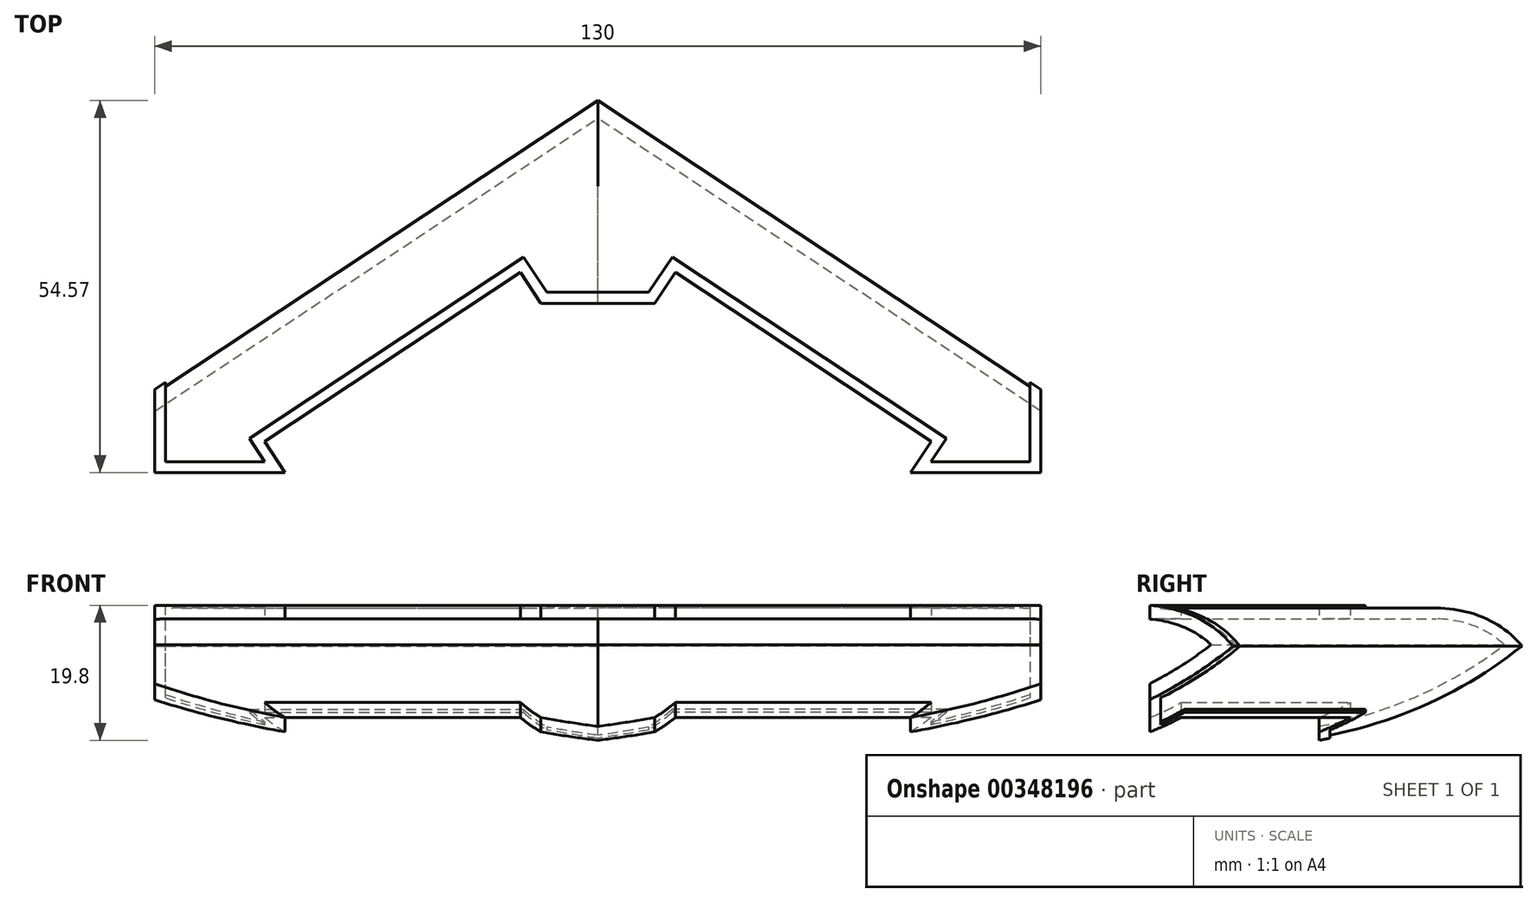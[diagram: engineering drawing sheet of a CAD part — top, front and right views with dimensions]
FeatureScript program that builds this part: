
annotation { "Feature Type Name" : "Feature", "Feature Type Description" : "" }
export const myFeature = defineFeature(function(context is Context, id is Id, definition is map)
    precondition{}
    {
        {
            var Q0;
            Q0=qCreatedBy(makeId("Top.planeOp"),FACE);
            var sketch = newSketch(context, id + "F0", { "sketchPlane" : qUnion([Q0])});
            skLineSegment(sketch, "E0", {"start": v(45.86, -2.86) * mm, "end": v(0, 27.5) * mm});
            skLineSegment(sketch, "E1", {"start": v(45.86, -2.86) * mm, "end": v(83.39, -27.7) * mm});
            skLineSegment(sketch, "E2", {"start": v(83.39, -27.7) * mm, "end": v(45.86, -27.7) * mm});
            skLineSegment(sketch, "E3", {"start": v(45.86, -27.7) * mm, "end": v(8.34, -2.86) * mm});
            skLineSegment(sketch, "E4", {"start": v(0, 27.5) * mm, "end": v(-20.1, -2.86) * mm});
            skLineSegment(sketch, "E5", {"start": v(-20.1, -2.86) * mm, "end": v(8.34, -2.86) * mm});
            skSolve(sketch);
        }
        {
            var Q0;
            Q0=makeQuery(id+"F0.imprint","IMPRINT",FACE,{"disambiguationData":[TD([[makeQuery(id+"F0.imprint","IMPRINT",EDGE,{"derivedFrom":sQuery(id+"F0.wireOp",EDGE,"E0")}),1.0]])]});
            extrude(context, id + "F1", {"entities" : qUnion([Q0]), "depth" : 21 * mm, "offsetDistance" : 25 * mm});
        }
        {
            var Q0;
            Q0=makeQuery(id+"F1.opExtrude","SWEPT_FACE",FACE,{"disambiguationData":[OSD([sQuery(id+"F0.wireOp",EDGE,"E4")])]});
            var sketch = newSketch(context, id + "F2", { "sketchPlane" : qUnion([Q0])});
            skLineSegment(sketch, "E6", {"start": v(-22.93, 21) * mm, "end": v(-22.93, 15) * mm});
            skLineSegment(sketch, "E7", {"start": v(-22.93, 21) * mm, "end": v(-11.93, 21) * mm});
            skArc(sketch, "E8", {"start": v(-11.93, 21) * mm, "mid": v(-18.2, 19.4) * mm, "end": v(-22.93, 15) * mm});
            skArc(sketch, "E9", {"start": v(-22.93, 15) * mm, "mid": v(-6.21, 3.9) * mm, "end": v(13.47, 0) * mm});
            skLineSegment(sketch, "E10", {"start": v(-11.93, 21) * mm, "end": v(13.47, 21) * mm});
            skArc(sketch, "E11.0", {"start": v(-20.27, 15.22) * mm, "mid": v(-4.65, 5.42) * mm, "end": v(13.47, 2) * mm});
            skArc(sketch, "E11.1", {"start": v(-11.93, 19) * mm, "mid": v(-16.5, 18.01) * mm, "end": v(-20.27, 15.22) * mm});
            skLineSegment(sketch, "E11.2", {"start": v(-11.93, 19) * mm, "end": v(13.47, 19) * mm});
            skSolve(sketch);
        }
        {
            var Q0;
            {var subQ0=sQuery(id+"F2.wireOp",EDGE,"E9");Q0=makeQuery(id+"F2.imprint","IMPRINT",FACE,{"disambiguationData":[TD([[makeQuery(id+"F2.imprint","IMPRINT",EDGE,{"derivedFrom":subQ0}),-1.0]])]});}
            var Q1;
            Q1=makeQuery(id+"F2.imprint","IMPRINT",FACE,{"disambiguationData":[TD([[makeQuery(id+"F2.imprint","IMPRINT",EDGE,{"derivedFrom":sQuery(id+"F2.wireOp",EDGE,"E6")}),1.0]])]});
            var Q2;
            {var subQ0=sQuery(id+"F2.wireOp",EDGE,"E11.0");Q2=makeQuery(id+"F2.imprint","IMPRINT",FACE,{"disambiguationData":[TD([[makeQuery(id+"F2.imprint","IMPRINT",EDGE,{"derivedFrom":subQ0}),1.0]])]});}
            extrude(context, id + "F3", {"entities" : qUnion([Q0, Q1, Q2]), "operationType" : NewBodyOperationType.REMOVE, "oppositeDirection" : true, "depth" : 150 * mm, "offsetDistance" : 25 * mm});
        }
        {
            var Q0;
            Q0=makeQuery(id+"F3.boolean.opBoolean","SPLIT",FACE,{"disambiguationData":[TD([makeQuery(id+"F3.opExtrude","SWEPT_FACE",FACE,{"disambiguationData":[OSD([sQuery(id+"F2.wireOp",EDGE,"E9")])]})])],"derivedFrom":makeQuery(id+"F1.opExtrude","SWEPT_FACE",FACE,{"disambiguationData":[OSD([sQuery(id+"F0.wireOp",EDGE,"E5")])]})});
            var sketch = newSketch(context, id + "F4", { "sketchPlane" : qUnion([Q0])});
            skLineSegment(sketch, "E12", {"start": v(0, 0) * mm, "end": v(0, 26.18) * mm});
            skLineSegment(sketch, "E13", {"start": v(0, 26.18) * mm, "end": v(-32.23, 26.18) * mm});
            skLineSegment(sketch, "E14", {"start": v(-32.23, 26.18) * mm, "end": v(-32.23, -6.17) * mm});
            skLineSegment(sketch, "E15", {"start": v(-32.23, -6.17) * mm, "end": v(0, -6.17) * mm});
            skLineSegment(sketch, "E16", {"start": v(0, -6.17) * mm, "end": v(0, 0) * mm});
            skSolve(sketch);
        }
        {
            var Q0;
            Q0 = qSketchRegion(id + "F4", true);
            extrude(context, id + "F5", {"entities" : qUnion([Q0]), "operationType" : NewBodyOperationType.REMOVE, "oppositeDirection" : true, "depth" : 31 * mm, "offsetDistance" : 25 * mm});
        }
        {
            var Q0;
            Q0=makeQuery(id+"F1.opExtrude","SWEPT_BODY",BODY,{"disambiguationData":[OSD([sQuery(id+"F0.wireOp",EDGE,"E0"),sQuery(id+"F0.wireOp",EDGE,"E1"),sQuery(id+"F0.wireOp",EDGE,"E2"),sQuery(id+"F0.wireOp",EDGE,"E3"),sQuery(id+"F0.wireOp",EDGE,"E4"),sQuery(id+"F0.wireOp",EDGE,"E5")])]});
            var Q1;
            Q1=makeQuery(id+"F5.boolean.opBoolean","COPY",FACE,{"derivedFrom":makeQuery(id+"F5.opExtrude","SWEPT_FACE",FACE,{"disambiguationData":[OSD([sQuery(id+"F4.wireOp",EDGE,"E12"),sQuery(id+"F4.wireOp",EDGE,"E16")])]})});
            mirror(context, id + "F6", {"operationType" : NewBodyOperationType.ADD, "entities" : qUnion([Q0]), "mirrorPlane" : qUnion([Q1])});
        }
        {
            var Q0;
            Q0=makeQuery(id+"F1.opExtrude","SWEPT_FACE",FACE,{"disambiguationData":[OSD([sQuery(id+"F0.wireOp",EDGE,"E2")])]});
            var sketch = newSketch(context, id + "F7", { "sketchPlane" : qUnion([Q0])});
            skLineSegment(sketch, "E17", {"start": v(-65, -2.93) * mm, "end": v(-65, 32.07) * mm});
            skLineSegment(sketch, "E18", {"start": v(-65, 32.07) * mm, "end": v(0, 32.07) * mm});
            skLineSegment(sketch, "E19", {"start": v(0, 32.07) * mm, "end": v(65, 32.07) * mm});
            skLineSegment(sketch, "E20", {"start": v(65, 32.07) * mm, "end": v(65, -2.93) * mm});
            skLineSegment(sketch, "E21", {"start": v(-65, -2.93) * mm, "end": v(-93.7, -2.93) * mm});
            skLineSegment(sketch, "E22", {"start": v(-93.7, -2.93) * mm, "end": v(-93.7, 32.07) * mm});
            skLineSegment(sketch, "E23", {"start": v(-93.7, 32.07) * mm, "end": v(-65, 32.07) * mm});
            skLineSegment(sketch, "E24", {"start": v(65, -2.93) * mm, "end": v(96.8, -3.17) * mm});
            skPoint(sketch, "E24.endSnap0", {"position": v(63.46, -3.17) * mm});
            skLineSegment(sketch, "E25", {"start": v(96.8, -3.17) * mm, "end": v(96.8, 32.07) * mm});
            skLineSegment(sketch, "E26", {"start": v(96.8, 32.07) * mm, "end": v(65, 32.07) * mm});
            skSolve(sketch);
        }
        {
            var Q0;
            Q0 = qSketchRegion(id + "F7", true);
            extrude(context, id + "F8", {"entities" : qUnion([Q0]), "operationType" : NewBodyOperationType.REMOVE, "oppositeDirection" : true, "depth" : 25 * mm, "offsetDistance" : 25 * mm});
        }
        {
            var Q0;
            Q0=makeQuery(id+"F6.opPattern","COPY",FACE,{"derivedFrom":makeQuery(id+"F3.boolean.opBoolean","SPLIT",FACE,{"disambiguationData":[TD([makeQuery(id+"F3.opExtrude","SWEPT_FACE",FACE,{"disambiguationData":[OSD([sQuery(id+"F2.wireOp",EDGE,"E9")])]})])],"derivedFrom":makeQuery(id+"F1.opExtrude","SWEPT_FACE",FACE,{"disambiguationData":[OSD([sQuery(id+"F0.wireOp",EDGE,"E3")])]})}),"instanceName":"1"});
            extrude(context, id + "F9", {"entities" : qUnion([Q0]), "operationType" : NewBodyOperationType.REMOVE, "oppositeDirection" : true, "depth" : 25 * mm, "offsetDistance" : 25 * mm});
        }
        {
            var Q0;
            Q0=makeQuery(id+"F3.boolean.opBoolean","SPLIT",FACE,{"disambiguationData":[TD([makeQuery(id+"F3.opExtrude","SWEPT_FACE",FACE,{"disambiguationData":[OSD([sQuery(id+"F2.wireOp",EDGE,"E9")])]})])],"derivedFrom":makeQuery(id+"F1.opExtrude","SWEPT_FACE",FACE,{"disambiguationData":[OSD([sQuery(id+"F0.wireOp",EDGE,"E3")])]})});
            extrude(context, id + "F10", {"entities" : qUnion([Q0]), "operationType" : NewBodyOperationType.REMOVE, "oppositeDirection" : true, "depth" : 25 * mm, "offsetDistance" : 25 * mm});
        }
        {
            var Q0;
            Q0=makeQuery(id+"F10.boolean.opBoolean","COPY",FACE,{"derivedFrom":makeQuery(id+"F10.opExtrude","SWEPT_FACE",FACE,{"disambiguationData":[OSD([sQuery(id+"F0.wireOp",EDGE,"E3"),sQuery(id+"F2.wireOp",EDGE,"E11.0")])]})});
            var Q1;
            Q1=makeQuery(id+"F9.boolean.opBoolean","COPY",FACE,{"derivedFrom":makeQuery(id+"F9.opExtrude","SWEPT_FACE",FACE,{"disambiguationData":[OSD([sQuery(id+"F0.wireOp",EDGE,"E3"),sQuery(id+"F2.wireOp",EDGE,"E11.0")])]})});
            extrude(context, id + "F11", {"entities" : qUnion([Q0, Q1]), "operationType" : NewBodyOperationType.REMOVE, "oppositeDirection" : true, "depth" : 30 * mm, "offsetDistance" : 25 * mm});
        }
        {
            var Q0;
            {var subQ0=makeQuery(id+"F1.opExtrude","CAP_FACE",FACE,{"disambiguationData":[OSD([sQuery(id+"F0.wireOp",EDGE,"E0"),sQuery(id+"F0.wireOp",EDGE,"E1"),sQuery(id+"F0.wireOp",EDGE,"E2"),sQuery(id+"F0.wireOp",EDGE,"E3"),sQuery(id+"F0.wireOp",EDGE,"E4"),sQuery(id+"F0.wireOp",EDGE,"E5")])],"isStart":false});Q0=makeQuery(id+"F6.boolean.opBoolean","MERGE",FACE,{"derivedFrom":[subQ0,makeQuery(id+"F6.opPattern","COPY",FACE,{"derivedFrom":subQ0,"instanceName":"1"})]});}
            var Q1;
            Q1=makeQuery(id+"F6.opPattern","COPY",FACE,{"derivedFrom":makeQuery(id+"F3.boolean.opBoolean","COPY",FACE,{"derivedFrom":makeQuery(id+"F3.opExtrude","SWEPT_FACE",FACE,{"disambiguationData":[OSD([sQuery(id+"F2.wireOp",EDGE,"E8")])]})}),"instanceName":"1"});
            var Q2;
            Q2=makeQuery(id+"F3.boolean.opBoolean","COPY",FACE,{"derivedFrom":makeQuery(id+"F3.opExtrude","SWEPT_FACE",FACE,{"disambiguationData":[OSD([sQuery(id+"F2.wireOp",EDGE,"E8")])]})});
            var Q3;
            Q3=makeQuery(id+"F6.opPattern","COPY",FACE,{"derivedFrom":makeQuery(id+"F3.boolean.opBoolean","COPY",FACE,{"derivedFrom":makeQuery(id+"F3.opExtrude","SWEPT_FACE",FACE,{"disambiguationData":[OSD([sQuery(id+"F2.wireOp",EDGE,"E9")])]})}),"instanceName":"1"});
            var Q4;
            Q4=makeQuery(id+"F3.boolean.opBoolean","COPY",FACE,{"derivedFrom":makeQuery(id+"F3.opExtrude","SWEPT_FACE",FACE,{"disambiguationData":[OSD([sQuery(id+"F2.wireOp",EDGE,"E9")])]})});
            shell(context, id + "F12", {"entities" : qUnion([Q0, Q1, Q2, Q3, Q4]), "thickness" : 1.6 * mm});
        }
    });
